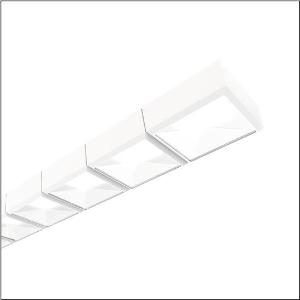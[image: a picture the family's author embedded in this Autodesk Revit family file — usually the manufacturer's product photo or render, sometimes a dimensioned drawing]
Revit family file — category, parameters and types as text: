
# Revit family: scriptus_r__11_5mz314d0twb_59a6
name_source: partatom
category: Lighting Fixtures
units: mm (PartAtom-declared; Revit-internal decimal feet)

## family parameters
Cut with Voids When Loaded = No
Host = Face
Light Source = No
Part Type = Normal
Room Calculation Point = No
Round Connector Dimension = Use Diameter
Shared = No

## types (1)
- --- (1 x LED 3000K+6500K / CRI = 80 (unbekannt), 3390 lm / 3600 lm, 3000K)
    Apparent Load = 106 VA
    CIE Flux Codes = 0 0 0 0 100 / 82 95 99 100 100
    Color Rendering = 80
    Color Temperature = 3000K
    Default Elevation = 1800 mm
    Description = Scriptus® 11, office luminaire, primary optical cover: lenses, CAT 2 (L<= 3000cd/m²), light emission: direct/indirect distribution, primary light characteristic: symmetric, installation type: suspended mounting, LED, rated luminous flux: 13.970lm, luminous efficacy: 128lm/W, light colour: 8tw, colour temperature: 3000..6500K, control gear: ECG DALI, with terminal, 5-pole, mains connection: 230V, AC, 50Hz, rated input power: 110W, LED, control gear: ECG DALI, housing, luminaire housing, of aluminium, traffic white (RAL 9016), length: 3.088mm, width: 114mm, height: 57mm, protection rating (complete): IP20, insulation class (complete): insulation class I (protective earthing), certification: CE, protection symbol: F, permissible operating ambient temperature: <= +25°C, standard: EN 50419, packaging unit: 1 piece
    Height = 57 mm
    Lamp = 1 x LED 3000K+6500K / CRI >= 80 (unbekannt)
    Lamp Light Flux = 3390 lm / 3600 lm
    Lamp count = 1
    Length = 3088 mm
    Luminous efficacy = 132 lm/W
    Manufacturer = Siteco
    ModVariant = No
    Model = 5MZ314D0TWB
    Mounting Place = Ceiling
    Mounting Type = Pendant
    Number of Poles = 1
    OnlyDefault = Yes
    Power Factor = 1
    Product Name = Scriptus® 11
    Product group = office luminaire | ceiling pendant
    ProductGroupID = 902
    Protection Class = Protection class I
    Protection Degree = IP 20
    RLX_Detail_Level = 1
    RLX_Emergency_Light_Flux = 0 lm
    RLX_Emergency_Type = 0
    RLX_Emergency_Type_DB = No
    RlxData = <blob elided: 32353 chars, md5=e85bd5c0>
    Socket = socket
    Standby Power = 0 W
    System Light Flux = 13980 lm
    System Power = 106 W
    Type Comments = individual setting: colour temperature 6500K
    Type Image = l_1004839.jpg
    URL = http://relux.com
    VarID = @adj_164644
    Voltage = 0 V
    Weight = 0.00 kg
    Width = 114 mm

## geometry (parser evidence)
native form markers: Blend x4, Sweep x20
no freeform markers — native parametric forms only
